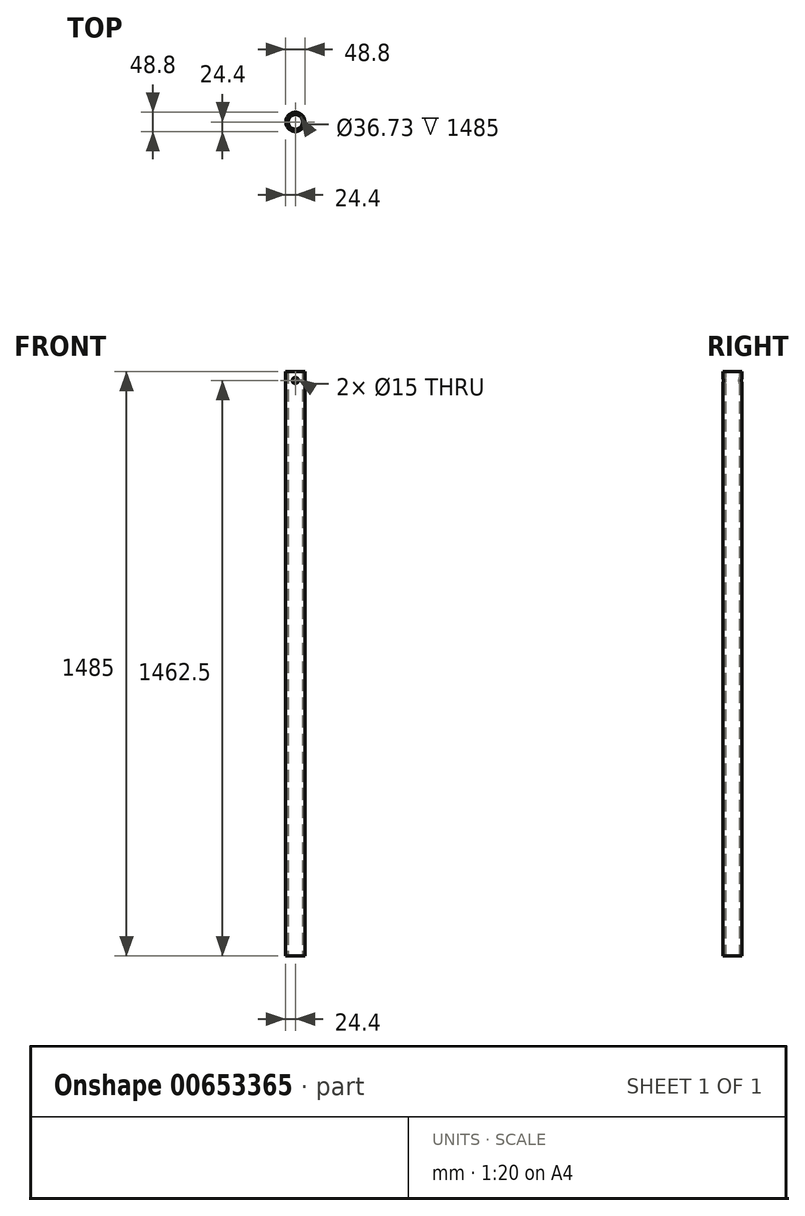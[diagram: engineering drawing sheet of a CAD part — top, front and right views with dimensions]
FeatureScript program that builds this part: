
annotation { "Feature Type Name" : "Feature", "Feature Type Description" : "" }
export const myFeature = defineFeature(function(context is Context, id is Id, definition is map)
    precondition{}
    {
        {
            var Q0;
            Q0=qCreatedBy(makeId("Top.planeOp"),FACE);
            var sketch = newSketch(context, id + "F0", { "sketchPlane" : qUnion([Q0])});
            skCircle(sketch, "E0", {"center": v(0, 0) * mm, "radius": 24.4 * mm});
            skCircle(sketch, "E1", {"center": v(0, 0) * mm, "radius": 18.37 * mm});
            skSolve(sketch);
        }
        {
            var Q0;
            Q0=qSketchRegion(id+"F0",true);
            extrude(context, id + "F1", {"entities" : qUnion([Q0]), "depth" : 60 * mm, "offsetDistance" : 25 * mm});
        }
        {
            var Q0;
            Q0=qCreatedBy(makeId("Top.planeOp"),FACE);
            var sketch = newSketch(context, id + "F2", { "sketchPlane" : qUnion([Q0])});
            skCircle(sketch, "E2.0", {"center": v(0, 0) * mm, "radius": 24.4 * mm});
            skCircle(sketch, "E3.0", {"center": v(0, 0) * mm, "radius": 18.37 * mm});
            skSolve(sketch);
        }
        {
            var Q0;
            Q0=qSketchRegion(id+"F2",true);
            extrude(context, id + "F3", {"entities" : qUnion([Q0]), "operationType" : NewBodyOperationType.ADD, "oppositeDirection" : true, "depth" : 1425 * mm, "offsetDistance" : 25 * mm});
        }
        {
            var Q0;
            Q0=qCreatedBy(makeId("Front.planeOp"),FACE);
            var sketch = newSketch(context, id + "F4", { "sketchPlane" : qUnion([Q0])});
            skLineSegment(sketch, "E4", {"start": v(0, 0) * mm, "end": v(0, 70.78) * mm, "construction": true});
            skCircle(sketch, "E5", {"center": v(0, 37.5) * mm, "radius": 7.5 * mm});
            skPoint(sketch, "E6.orphan", {"position": v(-23.77, 60) * mm});
            skPoint(sketch, "E7.0.end.orphan", {"position": v(23.77, 60) * mm});
            skPoint(sketch, "E7.0.start.orphan", {"position": v(0, 60) * mm});
            skLineSegment(sketch, "E8.0", {"start": v(-24.4, 60) * mm, "end": v(24.4, 60) * mm, "construction": true});
            skSolve(sketch);
        }
        {
            var Q0;
            Q0=qSketchRegion(id+"F4",true);
            extrude(context, id + "F5", {"entities" : qUnion([Q0]), "operationType" : NewBodyOperationType.REMOVE, "endBound" : BoundingType.THROUGH_ALL, "oppositeDirection" : true, "depth" : 25 * mm, "offsetDistance" : 25 * mm, "hasSecondDirection" : true, "secondDirectionBound" : BoundingType.THROUGH_ALL, "secondDirectionOppositeDirection" : false, "secondDirectionDepth" : 25 * mm});
        }
    });
